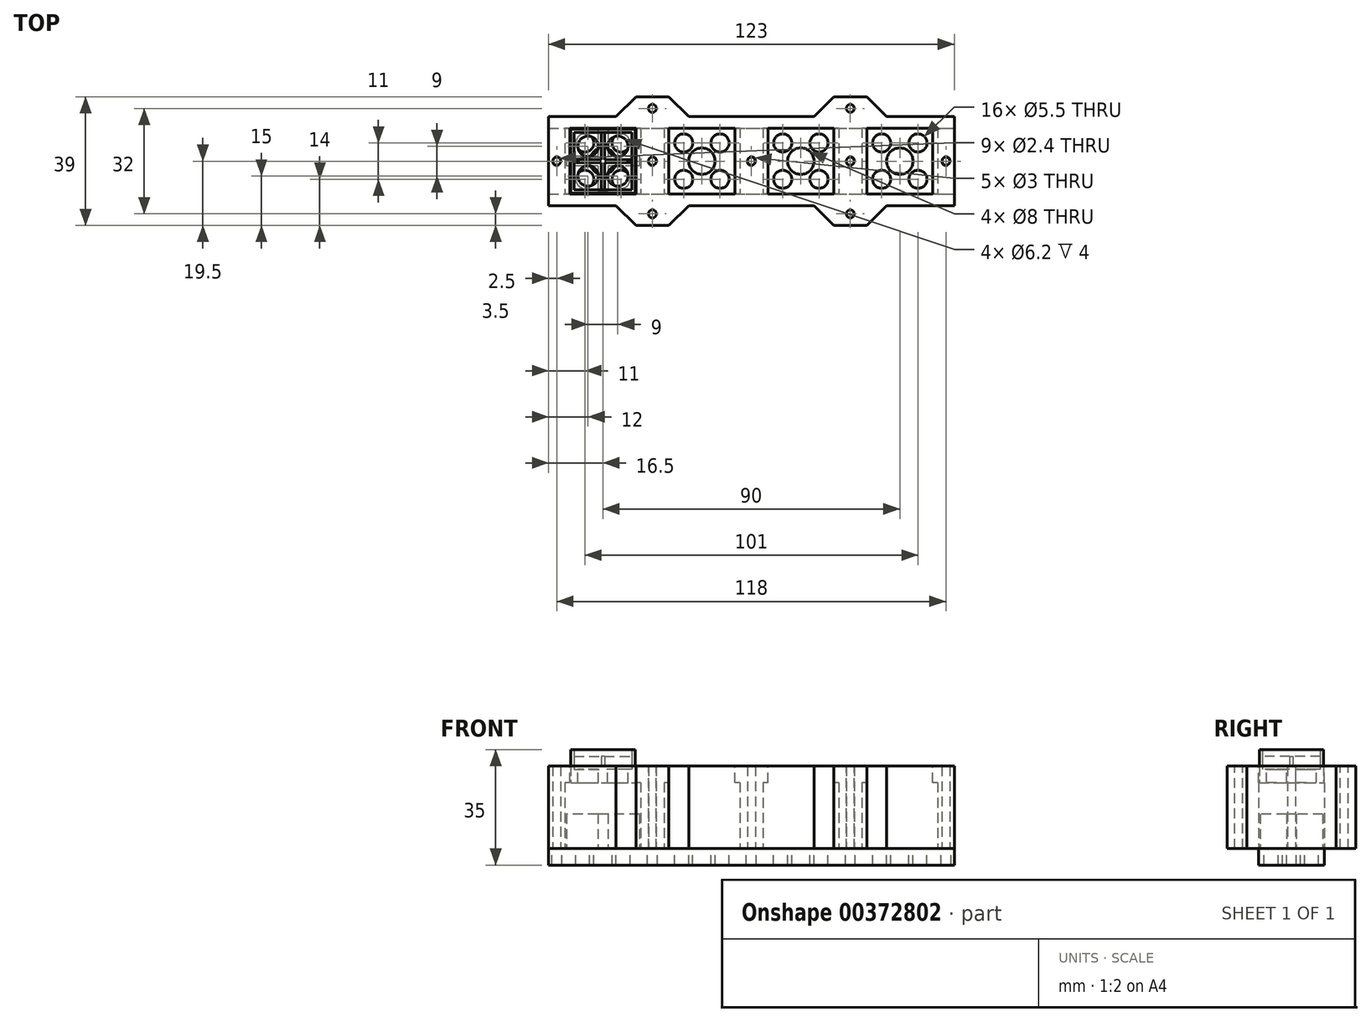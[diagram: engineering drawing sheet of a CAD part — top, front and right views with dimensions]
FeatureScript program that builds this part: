
annotation { "Feature Type Name" : "Feature", "Feature Type Description" : "" }
export const myFeature = defineFeature(function(context is Context, id is Id, definition is map)
    precondition{}
    {
        {
            var Q0;
            Q0=qCreatedBy(makeId("Top.planeOp"),FACE);
            var sketch = newSketch(context, id + "F0", { "sketchPlane" : qUnion([Q0])});
            skPoint(sketch, "E0.middle", {"position": v(0, 0) * mm});
            skLineSegment(sketch, "E1.bottom", {"start": v(9.75, -9.75) * mm, "end": v(-9.75, -9.75) * mm});
            skLineSegment(sketch, "E1.top", {"start": v(9.75, 9.75) * mm, "end": v(-9.75, 9.75) * mm});
            skLineSegment(sketch, "E1.left", {"start": v(9.75, -9.75) * mm, "end": v(9.75, 9.75) * mm});
            skLineSegment(sketch, "E1.right", {"start": v(-9.75, -9.75) * mm, "end": v(-9.75, 9.75) * mm});
            skSolve(sketch);
        }
        {
            var Q0;
            Q0=qSketchRegion(id+"F0",true);
            extrude(context, id + "F1", {"entities" : qUnion([Q0]), "depth" : 13 * mm, "offsetDistance" : 25 * mm});
        }
        {
            var Q0;
            Q0=makeQuery(id+"F1.opExtrude","CAP_FACE",FACE,{"disambiguationData":[OSD([sQuery(id+"F0.wireOp",EDGE,"E1.bottom"),sQuery(id+"F0.wireOp",EDGE,"E1.top"),sQuery(id+"F0.wireOp",EDGE,"E1.left"),sQuery(id+"F0.wireOp",EDGE,"E1.right")])],"isStart":false});
            var sketch = newSketch(context, id + "F2", { "sketchPlane" : qUnion([Q0])});
            skLineSegment(sketch, "E2.bottom", {"start": v(9.75, -9.75) * mm, "end": v(-9.75, -9.75) * mm});
            skLineSegment(sketch, "E2.top", {"start": v(9.75, 9.75) * mm, "end": v(-9.75, 9.75) * mm});
            skLineSegment(sketch, "E2.left", {"start": v(9.75, -9.75) * mm, "end": v(9.75, 9.75) * mm});
            skLineSegment(sketch, "E2.right", {"start": v(-9.75, -9.75) * mm, "end": v(-9.75, 9.75) * mm});
            skPoint(sketch, "E2.middle", {"position": v(0, 0) * mm});
            skLineSegment(sketch, "E3.bottom", {"start": v(8.75, -8.75) * mm, "end": v(-8.75, -8.75) * mm});
            skLineSegment(sketch, "E3.top", {"start": v(8.75, 8.75) * mm, "end": v(-8.75, 8.75) * mm});
            skLineSegment(sketch, "E3.left", {"start": v(8.75, -8.75) * mm, "end": v(8.75, 8.75) * mm});
            skLineSegment(sketch, "E3.right", {"start": v(-8.75, -8.75) * mm, "end": v(-8.75, 8.75) * mm});
            skSolve(sketch);
        }
        {
            var Q0;
            Q0=qSketchRegion(id+"F2",true);
            extrude(context, id + "F3", {"entities" : qUnion([Q0]), "operationType" : NewBodyOperationType.ADD, "depth" : 6 * mm, "offsetDistance" : 25 * mm});
        }
        {
            var Q0;
            Q0=makeQuery(id+"F1.opExtrude","CAP_FACE",FACE,{"disambiguationData":[OSD([sQuery(id+"F0.wireOp",EDGE,"E1.bottom"),sQuery(id+"F0.wireOp",EDGE,"E1.top"),sQuery(id+"F0.wireOp",EDGE,"E1.left"),sQuery(id+"F0.wireOp",EDGE,"E1.right")])],"isStart":false});
            var sketch = newSketch(context, id + "F4", { "sketchPlane" : qUnion([Q0])});
            skLineSegment(sketch, "E4.bottom", {"start": v(-0.5, 8.75) * mm, "end": v(0.5, 8.75) * mm});
            skLineSegment(sketch, "E4.top", {"start": v(-0.5, -8.75) * mm, "end": v(0.5, -8.75) * mm});
            skLineSegment(sketch, "E4.left", {"start": v(-0.5, 8.75) * mm, "end": v(-0.5, 0.5) * mm});
            skLineSegment(sketch, "E4.right", {"start": v(0.5, 8.75) * mm, "end": v(0.5, 0.5) * mm});
            skLineSegment(sketch, "E5.bottom", {"start": v(-8.75, 0.5) * mm, "end": v(-0.5, 0.5) * mm});
            skLineSegment(sketch, "E5.top", {"start": v(-8.75, -0.5) * mm, "end": v(-0.5, -0.5) * mm});
            skLineSegment(sketch, "E5.left", {"start": v(-8.75, 0.5) * mm, "end": v(-8.75, -0.5) * mm});
            skLineSegment(sketch, "E5.right", {"start": v(8.75, 0.5) * mm, "end": v(8.75, -0.5) * mm});
            skLineSegment(sketch, "E6.trimOffspring", {"start": v(-0.5, -0.5) * mm, "end": v(-0.5, -8.75) * mm});
            skLineSegment(sketch, "E7.trimOffspring", {"start": v(0.5, -0.5) * mm, "end": v(0.5, -8.75) * mm});
            skLineSegment(sketch, "E8.trimOffspring", {"start": v(0.5, 0.5) * mm, "end": v(8.75, 0.5) * mm});
            skLineSegment(sketch, "E9.trimOffspring", {"start": v(0.5, -0.5) * mm, "end": v(8.75, -0.5) * mm});
            skSolve(sketch);
        }
        {
            var Q0;
            Q0=qSketchRegion(id+"F4",true);
            extrude(context, id + "F5", {"entities" : qUnion([Q0]), "operationType" : NewBodyOperationType.ADD, "depth" : 4 * mm, "offsetDistance" : 25 * mm});
        }
        {
            var Q0;
            Q0=makeQuery(id+"F1.opExtrude","CAP_FACE",FACE,{"disambiguationData":[OSD([sQuery(id+"F0.wireOp",EDGE,"E1.bottom"),sQuery(id+"F0.wireOp",EDGE,"E1.top"),sQuery(id+"F0.wireOp",EDGE,"E1.left"),sQuery(id+"F0.wireOp",EDGE,"E1.right")])],"isStart":false});
            var sketch = newSketch(context, id + "F6", { "sketchPlane" : qUnion([Q0])});
            skCircle(sketch, "E10", {"center": v(-4.5, 4.5) * mm, "radius": 3.1 * mm});
            skCircle(sketch, "E11", {"center": v(-4.5, -4.5) * mm, "radius": 3.1 * mm});
            skCircle(sketch, "E12", {"center": v(4.5, 4.5) * mm, "radius": 3.1 * mm});
            skCircle(sketch, "E13", {"center": v(4.5, -4.5) * mm, "radius": 3.1 * mm});
            skSolve(sketch);
        }
        {
            var Q0;
            Q0=qSketchRegion(id+"F6",true);
            extrude(context, id + "F7", {"entities" : qUnion([Q0]), "operationType" : NewBodyOperationType.REMOVE, "oppositeDirection" : true, "depth" : 19 * mm, "offsetDistance" : 25 * mm});
        }
        {
            var Q0;
            Q0=makeQuery(id+"F1.opExtrude","CAP_FACE",FACE,{"disambiguationData":[OSD([sQuery(id+"F0.wireOp",EDGE,"E1.bottom"),sQuery(id+"F0.wireOp",EDGE,"E1.top"),sQuery(id+"F0.wireOp",EDGE,"E1.left"),sQuery(id+"F0.wireOp",EDGE,"E1.right")])],"isStart":true});
            var sketch = newSketch(context, id + "F8", { "sketchPlane" : qUnion([Q0])});
            skLineSegment(sketch, "E14.bottom", {"start": v(-9.75, -9.75) * mm, "end": v(-11.25, -9.75) * mm});
            skLineSegment(sketch, "E14.top", {"start": v(-9.75, 9.75) * mm, "end": v(-11.25, 9.75) * mm});
            skLineSegment(sketch, "E14.left", {"start": v(-9.75, -9.75) * mm, "end": v(-9.75, 9.75) * mm});
            skLineSegment(sketch, "E14.right", {"start": v(-11.25, -9.75) * mm, "end": v(-11.25, 9.75) * mm});
            skLineSegment(sketch, "E15.bottom", {"start": v(9.75, -9.75) * mm, "end": v(11.25, -9.75) * mm});
            skLineSegment(sketch, "E15.top", {"start": v(9.75, 9.75) * mm, "end": v(11.25, 9.75) * mm});
            skLineSegment(sketch, "E15.left", {"start": v(9.75, -9.75) * mm, "end": v(9.75, 9.75) * mm});
            skLineSegment(sketch, "E15.right", {"start": v(11.25, -9.75) * mm, "end": v(11.25, 9.75) * mm});
            skSolve(sketch);
        }
        {
            var Q0;
            Q0=qSketchRegion(id+"F8",true);
            extrude(context, id + "F9", {"entities" : qUnion([Q0]), "operationType" : NewBodyOperationType.ADD, "oppositeDirection" : true, "depth" : 9 * mm, "offsetDistance" : 25 * mm});
        }
        {
            var Q0;
            Q0=makeQuery(id+"F9.boolean.opBoolean","MERGE",FACE,{"derivedFrom":[makeQuery(id+"F1.opExtrude","CAP_FACE",FACE,{"disambiguationData":[OSD([sQuery(id+"F0.wireOp",EDGE,"E1.bottom"),sQuery(id+"F0.wireOp",EDGE,"E1.top"),sQuery(id+"F0.wireOp",EDGE,"E1.left"),sQuery(id+"F0.wireOp",EDGE,"E1.right")])],"isStart":true}),makeQuery(id+"F9.opExtrude","CAP_FACE",FACE,{"disambiguationData":[OSD([sQuery(id+"F8.wireOp",EDGE,"E14.bottom"),sQuery(id+"F8.wireOp",EDGE,"E14.top"),sQuery(id+"F8.wireOp",EDGE,"E14.left"),sQuery(id+"F8.wireOp",EDGE,"E14.right")])],"isStart":true}),makeQuery(id+"F9.opExtrude","CAP_FACE",FACE,{"disambiguationData":[OSD([sQuery(id+"F8.wireOp",EDGE,"E15.bottom"),sQuery(id+"F8.wireOp",EDGE,"E15.top"),sQuery(id+"F8.wireOp",EDGE,"E15.left"),sQuery(id+"F8.wireOp",EDGE,"E15.right")])],"isStart":true})]});
            var sketch = newSketch(context, id + "F10", { "sketchPlane" : qUnion([Q0])});
            skCircle(sketch, "E16", {"center": v(0, 0) * mm, "radius": 2.55 * mm});
            skSolve(sketch);
        }
        {
            var Q0;
            Q0=qSketchRegion(id+"F10",true);
            extrude(context, id + "F11", {"entities" : qUnion([Q0]), "operationType" : NewBodyOperationType.REMOVE, "oppositeDirection" : true, "depth" : 3 * mm, "offsetDistance" : 25 * mm});
        }
        {
            var Q0;
            Q0=qCreatedBy(makeId("Top.planeOp"),FACE);
            cPlane(context, id + "F12", {"entities" : qUnion([Q0]), "cplaneType" : CPlaneType.OFFSET, "offset" : 14 * mm, "width" : 150 * mm, "height" : 150 * mm});
        }
        {
            var Q0;
            Q0=qCreatedBy(id+"F12.planeOp",FACE);
            var sketch = newSketch(context, id + "F13", { "sketchPlane" : qUnion([Q0])});
            skPoint(sketch, "E17.middle", {"position": v(0, 0) * mm});
            skLineSegment(sketch, "E18.bottom", {"start": v(10, -10) * mm, "end": v(-10, -10) * mm});
            skLineSegment(sketch, "E18.top", {"start": v(10, 10) * mm, "end": v(-10, 10) * mm});
            skLineSegment(sketch, "E18.left", {"start": v(10, -10) * mm, "end": v(10, 10) * mm});
            skLineSegment(sketch, "E18.right", {"start": v(-10, -10) * mm, "end": v(-10, 10) * mm});
            skLineSegment(sketch, "E19.bottom", {"start": v(40, -10) * mm, "end": v(20, -10) * mm});
            skLineSegment(sketch, "E19.top", {"start": v(40, 10) * mm, "end": v(20, 10) * mm});
            skLineSegment(sketch, "E19.left", {"start": v(40, -10) * mm, "end": v(40, 10) * mm});
            skLineSegment(sketch, "E19.right", {"start": v(20, -10) * mm, "end": v(20, 10) * mm});
            skPoint(sketch, "E19.middle", {"position": v(30, 0) * mm});
            skLineSegment(sketch, "E20.bottom", {"start": v(70, -10) * mm, "end": v(50, -10) * mm});
            skLineSegment(sketch, "E20.top", {"start": v(70, 10) * mm, "end": v(50, 10) * mm});
            skLineSegment(sketch, "E20.left", {"start": v(70, -10) * mm, "end": v(70, 10) * mm});
            skLineSegment(sketch, "E20.right", {"start": v(50, -10) * mm, "end": v(50, 10) * mm});
            skPoint(sketch, "E20.middle", {"position": v(60, 0) * mm});
            skLineSegment(sketch, "E21.bottom", {"start": v(100, -10) * mm, "end": v(80, -10) * mm});
            skLineSegment(sketch, "E21.top", {"start": v(100, 10) * mm, "end": v(80, 10) * mm});
            skLineSegment(sketch, "E21.left", {"start": v(100, -10) * mm, "end": v(100, 10) * mm});
            skLineSegment(sketch, "E21.right", {"start": v(80, -10) * mm, "end": v(80, 10) * mm});
            skPoint(sketch, "E21.middle", {"position": v(90, 0) * mm});
            skLineSegment(sketch, "E22.bottom", {"start": v(10, 13.5) * mm, "end": v(20, 13.5) * mm});
            skLineSegment(sketch, "E22.top", {"start": v(10, 19.5) * mm, "end": v(20, 19.5) * mm});
            skLineSegment(sketch, "E22.left", {"start": v(10, 13.5) * mm, "end": v(10, 19.5) * mm});
            skLineSegment(sketch, "E22.right", {"start": v(20, 13.5) * mm, "end": v(20, 19.5) * mm});
            skLineSegment(sketch, "E23.bottom", {"start": v(10, -13.5) * mm, "end": v(20, -13.5) * mm});
            skLineSegment(sketch, "E23.top", {"start": v(10, -19.5) * mm, "end": v(20, -19.5) * mm});
            skLineSegment(sketch, "E23.left", {"start": v(10, -13.5) * mm, "end": v(10, -19.5) * mm});
            skLineSegment(sketch, "E23.right", {"start": v(20, -13.5) * mm, "end": v(20, -19.5) * mm});
            skLineSegment(sketch, "E24.bottom", {"start": v(106.5, -13.5) * mm, "end": v(-16.5, -13.5) * mm});
            skLineSegment(sketch, "E24.top", {"start": v(106.5, 13.5) * mm, "end": v(-16.5, 13.5) * mm});
            skLineSegment(sketch, "E24.left", {"start": v(106.5, -13.5) * mm, "end": v(106.5, 13.5) * mm});
            skLineSegment(sketch, "E24.right", {"start": v(-16.5, -13.5) * mm, "end": v(-16.5, 13.5) * mm});
            skPoint(sketch, "E24.middle", {"position": v(45, 0) * mm});
            skLineSegment(sketch, "E25.bottom", {"start": v(70, 13.5) * mm, "end": v(80, 13.5) * mm});
            skLineSegment(sketch, "E25.top", {"start": v(70, 19.5) * mm, "end": v(80, 19.5) * mm});
            skLineSegment(sketch, "E25.left", {"start": v(70, 13.5) * mm, "end": v(70, 19.5) * mm});
            skLineSegment(sketch, "E25.right", {"start": v(80, 13.5) * mm, "end": v(80, 19.5) * mm});
            skLineSegment(sketch, "E26.bottom", {"start": v(70, -13.5) * mm, "end": v(80, -13.5) * mm});
            skLineSegment(sketch, "E26.top", {"start": v(70, -19.5) * mm, "end": v(80, -19.5) * mm});
            skLineSegment(sketch, "E26.left", {"start": v(70, -13.5) * mm, "end": v(70, -19.5) * mm});
            skLineSegment(sketch, "E26.right", {"start": v(80, -13.5) * mm, "end": v(80, -19.5) * mm});
            skSolve(sketch);
        }
        {
            var Q0;
            Q0=qSketchRegion(id+"F13",true);
            extrude(context, id + "F14", {"entities" : qUnion([Q0]), "oppositeDirection" : true, "depth" : 25 * mm, "offsetDistance" : 25 * mm});
        }
        {
            var Q0;
            Q0=makeQuery(id+"F14.opExtrude","CAP_FACE",FACE,{"disambiguationData":[OSD([sQuery(id+"F13.wireOp",EDGE,"E17.bottom"),sQuery(id+"F13.wireOp",EDGE,"E17.top"),sQuery(id+"F13.wireOp",EDGE,"E17.left"),sQuery(id+"F13.wireOp",EDGE,"E17.right"),sQuery(id+"F13.wireOp",EDGE,"E18.bottom"),sQuery(id+"F13.wireOp",EDGE,"E18.top"),sQuery(id+"F13.wireOp",EDGE,"E18.left"),sQuery(id+"F13.wireOp",EDGE,"E18.right")])],"isStart":false});
            var sketch = newSketch(context, id + "F15", { "sketchPlane" : qUnion([Q0])});
            skLineSegment(sketch, "E27.bottom", {"start": v(11.5, -10) * mm, "end": v(-11.5, -10) * mm});
            skLineSegment(sketch, "E27.top", {"start": v(11.5, 10) * mm, "end": v(-11.5, 10) * mm});
            skLineSegment(sketch, "E27.left", {"start": v(11.5, -10) * mm, "end": v(11.5, 10) * mm});
            skLineSegment(sketch, "E27.right", {"start": v(-11.5, -10) * mm, "end": v(-11.5, 10) * mm});
            skPoint(sketch, "E27.middle", {"position": v(0, 0) * mm});
            skLineSegment(sketch, "E28.bottom", {"start": v(41.5, -10) * mm, "end": v(18.5, -10) * mm});
            skLineSegment(sketch, "E28.top", {"start": v(41.5, 10) * mm, "end": v(18.5, 10) * mm});
            skLineSegment(sketch, "E28.left", {"start": v(41.5, -10) * mm, "end": v(41.5, 10) * mm});
            skLineSegment(sketch, "E28.right", {"start": v(18.5, -10) * mm, "end": v(18.5, 10) * mm});
            skPoint(sketch, "E28.middle", {"position": v(30, 0) * mm});
            skPoint(sketch, "E28.middle.positionSnap0", {"position": v(20, 0) * mm});
            skPoint(sketch, "E28.middle.positionSnap1", {"position": v(30, 10) * mm});
            skPoint(sketch, "E28.centerSnap0", {"position": v(20, 0) * mm});
            skPoint(sketch, "E28.centerSnap1", {"position": v(30, 10) * mm});
            skLineSegment(sketch, "E29.bottom", {"start": v(71.5, -10) * mm, "end": v(48.5, -10) * mm});
            skLineSegment(sketch, "E29.top", {"start": v(71.5, 10) * mm, "end": v(48.5, 10) * mm});
            skLineSegment(sketch, "E29.left", {"start": v(71.5, -10) * mm, "end": v(71.5, 10) * mm});
            skLineSegment(sketch, "E29.right", {"start": v(48.5, -10) * mm, "end": v(48.5, 10) * mm});
            skPoint(sketch, "E29.middle", {"position": v(60, 0) * mm});
            skPoint(sketch, "E29.middle.positionSnap0", {"position": v(50, 0) * mm});
            skPoint(sketch, "E29.middle.positionSnap1", {"position": v(60, 10) * mm});
            skPoint(sketch, "E29.centerSnap0", {"position": v(50, 0) * mm});
            skPoint(sketch, "E29.centerSnap1", {"position": v(60, 10) * mm});
            skLineSegment(sketch, "E30.bottom", {"start": v(101.5, -10) * mm, "end": v(78.5, -10) * mm});
            skLineSegment(sketch, "E30.top", {"start": v(101.5, 10) * mm, "end": v(78.5, 10) * mm});
            skLineSegment(sketch, "E30.left", {"start": v(101.5, -10) * mm, "end": v(101.5, 10) * mm});
            skLineSegment(sketch, "E30.right", {"start": v(78.5, -10) * mm, "end": v(78.5, 10) * mm});
            skPoint(sketch, "E30.middle", {"position": v(90, 0) * mm});
            skPoint(sketch, "E30.middle.positionSnap0", {"position": v(90, 10) * mm});
            skPoint(sketch, "E30.centerSnap0", {"position": v(90, 10) * mm});
            skSolve(sketch);
        }
        {
            var Q0;
            Q0=qSketchRegion(id+"F15",true);
            extrude(context, id + "F16", {"entities" : qUnion([Q0]), "operationType" : NewBodyOperationType.REMOVE, "oppositeDirection" : true, "depth" : 20 * mm, "offsetDistance" : 25 * mm});
        }
        {
            var Q0;
            Q0=makeQuery(id+"F14.opExtrude","CAP_FACE",FACE,{"disambiguationData":[OSD([sQuery(id+"F13.wireOp",EDGE,"E18.bottom"),sQuery(id+"F13.wireOp",EDGE,"E18.top"),sQuery(id+"F13.wireOp",EDGE,"E18.left"),sQuery(id+"F13.wireOp",EDGE,"E18.right"),sQuery(id+"F13.wireOp",EDGE,"E19.bottom"),sQuery(id+"F13.wireOp",EDGE,"E19.top"),sQuery(id+"F13.wireOp",EDGE,"E19.left"),sQuery(id+"F13.wireOp",EDGE,"E19.right"),sQuery(id+"F13.wireOp",EDGE,"E20.bottom"),sQuery(id+"F13.wireOp",EDGE,"E20.top"),sQuery(id+"F13.wireOp",EDGE,"E20.left"),sQuery(id+"F13.wireOp",EDGE,"E20.right"),sQuery(id+"F13.wireOp",EDGE,"E21.bottom"),sQuery(id+"F13.wireOp",EDGE,"E21.top"),sQuery(id+"F13.wireOp",EDGE,"E21.left"),sQuery(id+"F13.wireOp",EDGE,"E21.right"),sQuery(id+"F13.wireOp",EDGE,"E22.top"),sQuery(id+"F13.wireOp",EDGE,"E22.left"),sQuery(id+"F13.wireOp",EDGE,"E22.right"),sQuery(id+"F13.wireOp",EDGE,"E23.top"),sQuery(id+"F13.wireOp",EDGE,"E23.left"),sQuery(id+"F13.wireOp",EDGE,"E23.right"),sQuery(id+"F13.wireOp",EDGE,"E24.bottom"),sQuery(id+"F13.wireOp",EDGE,"E24.top"),sQuery(id+"F13.wireOp",EDGE,"E24.left"),sQuery(id+"F13.wireOp",EDGE,"E24.right"),sQuery(id+"F13.wireOp",EDGE,"E25.top"),sQuery(id+"F13.wireOp",EDGE,"E25.left"),sQuery(id+"F13.wireOp",EDGE,"E25.right"),sQuery(id+"F13.wireOp",EDGE,"E26.top"),sQuery(id+"F13.wireOp",EDGE,"E26.left"),sQuery(id+"F13.wireOp",EDGE,"E26.right")])],"isStart":true});
            var sketch = newSketch(context, id + "F17", { "sketchPlane" : qUnion([Q0])});
            skCircle(sketch, "E31", {"center": v(15, 16) * mm, "radius": 1.2 * mm});
            skPoint(sketch, "E31.centerSnap0", {"position": v(15, 19.5) * mm});
            skCircle(sketch, "E32", {"center": v(15, -16) * mm, "radius": 1.2 * mm});
            skCircle(sketch, "E33", {"center": v(75, 16) * mm, "radius": 1.2 * mm});
            skPoint(sketch, "E33.centerSnap0", {"position": v(75, 19.5) * mm});
            skCircle(sketch, "E34", {"center": v(75, -16) * mm, "radius": 1.2 * mm});
            skSolve(sketch);
        }
        {
            var Q0;
            Q0=qSketchRegion(id+"F17",true);
            extrude(context, id + "F18", {"entities" : qUnion([Q0]), "operationType" : NewBodyOperationType.REMOVE, "oppositeDirection" : true, "depth" : 30 * mm, "offsetDistance" : 25 * mm});
        }
        {
            var Q0;
            Q0=makeQuery(id+"F14.opExtrude","CAP_FACE",FACE,{"disambiguationData":[OSD([sQuery(id+"F13.wireOp",EDGE,"E18.bottom"),sQuery(id+"F13.wireOp",EDGE,"E18.top"),sQuery(id+"F13.wireOp",EDGE,"E18.left"),sQuery(id+"F13.wireOp",EDGE,"E18.right"),sQuery(id+"F13.wireOp",EDGE,"E19.bottom"),sQuery(id+"F13.wireOp",EDGE,"E19.top"),sQuery(id+"F13.wireOp",EDGE,"E19.left"),sQuery(id+"F13.wireOp",EDGE,"E19.right"),sQuery(id+"F13.wireOp",EDGE,"E20.bottom"),sQuery(id+"F13.wireOp",EDGE,"E20.top"),sQuery(id+"F13.wireOp",EDGE,"E20.left"),sQuery(id+"F13.wireOp",EDGE,"E20.right"),sQuery(id+"F13.wireOp",EDGE,"E21.bottom"),sQuery(id+"F13.wireOp",EDGE,"E21.top"),sQuery(id+"F13.wireOp",EDGE,"E21.left"),sQuery(id+"F13.wireOp",EDGE,"E21.right"),sQuery(id+"F13.wireOp",EDGE,"E22.top"),sQuery(id+"F13.wireOp",EDGE,"E22.left"),sQuery(id+"F13.wireOp",EDGE,"E22.right"),sQuery(id+"F13.wireOp",EDGE,"E23.top"),sQuery(id+"F13.wireOp",EDGE,"E23.left"),sQuery(id+"F13.wireOp",EDGE,"E23.right"),sQuery(id+"F13.wireOp",EDGE,"E24.bottom"),sQuery(id+"F13.wireOp",EDGE,"E24.top"),sQuery(id+"F13.wireOp",EDGE,"E24.left"),sQuery(id+"F13.wireOp",EDGE,"E24.right"),sQuery(id+"F13.wireOp",EDGE,"E25.top"),sQuery(id+"F13.wireOp",EDGE,"E25.left"),sQuery(id+"F13.wireOp",EDGE,"E25.right"),sQuery(id+"F13.wireOp",EDGE,"E26.top"),sQuery(id+"F13.wireOp",EDGE,"E26.left"),sQuery(id+"F13.wireOp",EDGE,"E26.right")])],"isStart":false});
            var sketch = newSketch(context, id + "F19", { "sketchPlane" : qUnion([Q0])});
            skCircle(sketch, "E35", {"center": v(-14, 0) * mm, "radius": 1.2 * mm});
            skCircle(sketch, "E36", {"center": v(15, 0) * mm, "radius": 1.2 * mm});
            skCircle(sketch, "E37", {"center": v(45, 0) * mm, "radius": 1.2 * mm});
            skCircle(sketch, "E38", {"center": v(75, 0) * mm, "radius": 1.2 * mm});
            skCircle(sketch, "E39", {"center": v(104, 0) * mm, "radius": 1.2 * mm});
            skSolve(sketch);
        }
        {
            var Q0;
            Q0=qSketchRegion(id+"F19",true);
            extrude(context, id + "F20", {"entities" : qUnion([Q0]), "operationType" : NewBodyOperationType.REMOVE, "endBound" : BoundingType.THROUGH_ALL, "oppositeDirection" : true, "depth" : 10 * mm, "offsetDistance" : 25 * mm});
        }
        {
            var Q0;
            Q0=makeQuery(id+"F14.opExtrude","CAP_FACE",FACE,{"disambiguationData":[OSD([sQuery(id+"F13.wireOp",EDGE,"E18.bottom"),sQuery(id+"F13.wireOp",EDGE,"E18.top"),sQuery(id+"F13.wireOp",EDGE,"E18.left"),sQuery(id+"F13.wireOp",EDGE,"E18.right"),sQuery(id+"F13.wireOp",EDGE,"E19.bottom"),sQuery(id+"F13.wireOp",EDGE,"E19.top"),sQuery(id+"F13.wireOp",EDGE,"E19.left"),sQuery(id+"F13.wireOp",EDGE,"E19.right"),sQuery(id+"F13.wireOp",EDGE,"E20.bottom"),sQuery(id+"F13.wireOp",EDGE,"E20.top"),sQuery(id+"F13.wireOp",EDGE,"E20.left"),sQuery(id+"F13.wireOp",EDGE,"E20.right"),sQuery(id+"F13.wireOp",EDGE,"E21.bottom"),sQuery(id+"F13.wireOp",EDGE,"E21.top"),sQuery(id+"F13.wireOp",EDGE,"E21.left"),sQuery(id+"F13.wireOp",EDGE,"E21.right"),sQuery(id+"F13.wireOp",EDGE,"E22.top"),sQuery(id+"F13.wireOp",EDGE,"E22.left"),sQuery(id+"F13.wireOp",EDGE,"E22.right"),sQuery(id+"F13.wireOp",EDGE,"E23.top"),sQuery(id+"F13.wireOp",EDGE,"E23.left"),sQuery(id+"F13.wireOp",EDGE,"E23.right"),sQuery(id+"F13.wireOp",EDGE,"E24.bottom"),sQuery(id+"F13.wireOp",EDGE,"E24.top"),sQuery(id+"F13.wireOp",EDGE,"E24.left"),sQuery(id+"F13.wireOp",EDGE,"E24.right"),sQuery(id+"F13.wireOp",EDGE,"E25.top"),sQuery(id+"F13.wireOp",EDGE,"E25.left"),sQuery(id+"F13.wireOp",EDGE,"E25.right"),sQuery(id+"F13.wireOp",EDGE,"E26.top"),sQuery(id+"F13.wireOp",EDGE,"E26.left"),sQuery(id+"F13.wireOp",EDGE,"E26.right")])],"isStart":false});
            var sketch = newSketch(context, id + "F21", { "sketchPlane" : qUnion([Q0])});
            skCircle(sketch, "E40", {"center": v(-14, 0) * mm, "radius": 1.5 * mm});
            skCircle(sketch, "E41", {"center": v(15, 0) * mm, "radius": 1.5 * mm});
            skCircle(sketch, "E42", {"center": v(45, 0) * mm, "radius": 1.5 * mm});
            skCircle(sketch, "E43", {"center": v(75, 0) * mm, "radius": 1.5 * mm});
            skCircle(sketch, "E44", {"center": v(104, 0) * mm, "radius": 1.5 * mm});
            skCircle(sketch, "E45", {"center": v(0, 0) * mm, "radius": 4 * mm});
            skCircle(sketch, "E46", {"center": v(-5.5, 5.5) * mm, "radius": 2.75 * mm});
            skCircle(sketch, "E47", {"center": v(5.5, 5.5) * mm, "radius": 2.75 * mm});
            skCircle(sketch, "E48", {"center": v(-5.5, -5.5) * mm, "radius": 2.75 * mm});
            skCircle(sketch, "E49", {"center": v(5.5, -5.5) * mm, "radius": 2.75 * mm});
            skCircle(sketch, "E50.1.0.0", {"center": v(30, 0) * mm, "radius": 4 * mm});
            skCircle(sketch, "E50.1.0.1", {"center": v(35.5, -5.5) * mm, "radius": 2.75 * mm});
            skCircle(sketch, "E50.1.0.2", {"center": v(35.5, 5.5) * mm, "radius": 2.75 * mm});
            skCircle(sketch, "E50.1.0.3", {"center": v(24.5, 5.5) * mm, "radius": 2.75 * mm});
            skCircle(sketch, "E50.1.0.4", {"center": v(24.5, -5.5) * mm, "radius": 2.75 * mm});
            skCircle(sketch, "E50.2.0.0", {"center": v(60, 0) * mm, "radius": 4 * mm});
            skCircle(sketch, "E50.2.0.1", {"center": v(65.5, -5.5) * mm, "radius": 2.75 * mm});
            skCircle(sketch, "E50.2.0.2", {"center": v(65.5, 5.5) * mm, "radius": 2.75 * mm});
            skCircle(sketch, "E50.2.0.3", {"center": v(54.5, 5.5) * mm, "radius": 2.75 * mm});
            skCircle(sketch, "E50.2.0.4", {"center": v(54.5, -5.5) * mm, "radius": 2.75 * mm});
            skLineSegment(sketch, "E50.direction1", {"start": v(-5.5, -5.5) * mm, "end": v(24.5, -5.5) * mm, "construction": true});
            skCircle(sketch, "E51.0.3.0", {"center": v(90, 0) * mm, "radius": 4 * mm});
            skCircle(sketch, "E51.2.3.0", {"center": v(95.5, -5.5) * mm, "radius": 2.75 * mm});
            skCircle(sketch, "E51.4.3.0", {"center": v(95.5, 5.5) * mm, "radius": 2.75 * mm});
            skCircle(sketch, "E51.6.3.0", {"center": v(84.5, 5.5) * mm, "radius": 2.75 * mm});
            skCircle(sketch, "E51.8.3.0", {"center": v(84.5, -5.5) * mm, "radius": 2.75 * mm});
            skLineSegment(sketch, "E52.bottom", {"start": v(-16.5, -10) * mm, "end": v(106.5, -10) * mm});
            skLineSegment(sketch, "E52.top", {"start": v(-16.5, 10) * mm, "end": v(106.5, 10) * mm});
            skLineSegment(sketch, "E52.left", {"start": v(-16.5, -10) * mm, "end": v(-16.5, 10) * mm});
            skLineSegment(sketch, "E52.right", {"start": v(106.5, -10) * mm, "end": v(106.5, 10) * mm});
            skSolve(sketch);
        }
        {
            var Q0;
            Q0=qSketchRegion(id+"F21",true);
            extrude(context, id + "F22", {"entities" : qUnion([Q0]), "depth" : 5 * mm, "offsetDistance" : 25 * mm});
        }
        {
            var Q0;
            Q0=makeQuery(id+"F14.opExtrude","SWEPT_EDGE",EDGE,{"disambiguationData":[OSD([sQuery(id+"F13.wireOp",EDGE,"E23.left"),sQuery(id+"F13.wireOp",EDGE,"E24.bottom")])]});
            var Q1;
            Q1=makeQuery(id+"F14.opExtrude","SWEPT_EDGE",EDGE,{"disambiguationData":[OSD([sQuery(id+"F13.wireOp",EDGE,"E23.right"),sQuery(id+"F13.wireOp",EDGE,"E24.bottom")])]});
            var Q2;
            Q2=makeQuery(id+"F14.opExtrude","SWEPT_EDGE",EDGE,{"disambiguationData":[OSD([sQuery(id+"F13.wireOp",EDGE,"E24.bottom"),sQuery(id+"F13.wireOp",EDGE,"E26.bottom"),sQuery(id+"F13.wireOp",EDGE,"E26.left")])]});
            var Q3;
            Q3=makeQuery(id+"F14.opExtrude","SWEPT_EDGE",EDGE,{"disambiguationData":[OSD([sQuery(id+"F13.wireOp",EDGE,"E24.bottom"),sQuery(id+"F13.wireOp",EDGE,"E26.bottom"),sQuery(id+"F13.wireOp",EDGE,"E26.right")])]});
            var Q4;
            Q4=makeQuery(id+"F14.opExtrude","SWEPT_EDGE",EDGE,{"disambiguationData":[OSD([sQuery(id+"F13.wireOp",EDGE,"E22.left"),sQuery(id+"F13.wireOp",EDGE,"E24.top")])]});
            var Q5;
            Q5=makeQuery(id+"F14.opExtrude","SWEPT_EDGE",EDGE,{"disambiguationData":[OSD([sQuery(id+"F13.wireOp",EDGE,"E22.right"),sQuery(id+"F13.wireOp",EDGE,"E24.top")])]});
            var Q6;
            Q6=makeQuery(id+"F14.opExtrude","SWEPT_EDGE",EDGE,{"disambiguationData":[OSD([sQuery(id+"F13.wireOp",EDGE,"E24.top"),sQuery(id+"F13.wireOp",EDGE,"E25.bottom"),sQuery(id+"F13.wireOp",EDGE,"E25.left")])]});
            var Q7;
            Q7=makeQuery(id+"F14.opExtrude","SWEPT_EDGE",EDGE,{"disambiguationData":[OSD([sQuery(id+"F13.wireOp",EDGE,"E24.top"),sQuery(id+"F13.wireOp",EDGE,"E25.bottom"),sQuery(id+"F13.wireOp",EDGE,"E25.right")])]});
            chamfer(context, id + "F23", {"entities" : qUnion([Q0, Q1, Q2, Q3, Q4, Q5, Q6, Q7]), "width" : 6 * mm, "tangentPropagation" : true});
        }
        {
            var Q0;
            Q0=makeQuery(id+"F14.opExtrude","CAP_FACE",FACE,{"disambiguationData":[OSD([sQuery(id+"F13.wireOp",EDGE,"E18.bottom"),sQuery(id+"F13.wireOp",EDGE,"E18.top"),sQuery(id+"F13.wireOp",EDGE,"E18.left"),sQuery(id+"F13.wireOp",EDGE,"E18.right"),sQuery(id+"F13.wireOp",EDGE,"E19.bottom"),sQuery(id+"F13.wireOp",EDGE,"E19.top"),sQuery(id+"F13.wireOp",EDGE,"E19.left"),sQuery(id+"F13.wireOp",EDGE,"E19.right"),sQuery(id+"F13.wireOp",EDGE,"E20.bottom"),sQuery(id+"F13.wireOp",EDGE,"E20.top"),sQuery(id+"F13.wireOp",EDGE,"E20.left"),sQuery(id+"F13.wireOp",EDGE,"E20.right"),sQuery(id+"F13.wireOp",EDGE,"E21.bottom"),sQuery(id+"F13.wireOp",EDGE,"E21.top"),sQuery(id+"F13.wireOp",EDGE,"E21.left"),sQuery(id+"F13.wireOp",EDGE,"E21.right"),sQuery(id+"F13.wireOp",EDGE,"E22.top"),sQuery(id+"F13.wireOp",EDGE,"E22.left"),sQuery(id+"F13.wireOp",EDGE,"E22.right"),sQuery(id+"F13.wireOp",EDGE,"E23.top"),sQuery(id+"F13.wireOp",EDGE,"E23.left"),sQuery(id+"F13.wireOp",EDGE,"E23.right"),sQuery(id+"F13.wireOp",EDGE,"E24.bottom"),sQuery(id+"F13.wireOp",EDGE,"E24.top"),sQuery(id+"F13.wireOp",EDGE,"E24.left"),sQuery(id+"F13.wireOp",EDGE,"E24.right"),sQuery(id+"F13.wireOp",EDGE,"E25.top"),sQuery(id+"F13.wireOp",EDGE,"E25.left"),sQuery(id+"F13.wireOp",EDGE,"E25.right"),sQuery(id+"F13.wireOp",EDGE,"E26.top"),sQuery(id+"F13.wireOp",EDGE,"E26.left"),sQuery(id+"F13.wireOp",EDGE,"E26.right")])],"isStart":false});
            cPlane(context, id + "F24", {"entities" : qUnion([Q0]), "cplaneType" : CPlaneType.OFFSET, "offset" : 0 * mm, "width" : 150 * mm, "height" : 150 * mm});
        }
        {
            var Q0;
            Q0=qCreatedBy(id+"F24.planeOp",FACE);
            var sketch = newSketch(context, id + "F25", { "sketchPlane" : qUnion([Q0])});
            skLineSegment(sketch, "E53.bottom", {"start": v(1.5, -9.5) * mm, "end": v(-1.5, -9.5) * mm});
            skLineSegment(sketch, "E53.top", {"start": v(1.5, 9.5) * mm, "end": v(-1.5, 9.5) * mm});
            skLineSegment(sketch, "E53.left", {"start": v(1.5, -9.5) * mm, "end": v(1.5, 9.5) * mm});
            skLineSegment(sketch, "E53.right", {"start": v(-1.5, -9.5) * mm, "end": v(-1.5, 9.5) * mm});
            skPoint(sketch, "E53.middle", {"position": v(0, 0) * mm});
            skLineSegment(sketch, "E54.bottom", {"start": v(11, -1.5) * mm, "end": v(-11, -1.5) * mm});
            skLineSegment(sketch, "E54.top", {"start": v(11, 1.5) * mm, "end": v(-11, 1.5) * mm});
            skLineSegment(sketch, "E54.left", {"start": v(11, -1.5) * mm, "end": v(11, 1.5) * mm});
            skLineSegment(sketch, "E54.right", {"start": v(-11, -1.5) * mm, "end": v(-11, 1.5) * mm});
            skLineSegment(sketch, "E55.0", {"start": v(11.5, 10) * mm, "end": v(-11.5, 10) * mm});
            skLineSegment(sketch, "E55.1", {"start": v(11.5, -10) * mm, "end": v(11.5, 10) * mm});
            skPoint(sketch, "E56", {"position": v(11.5, 0) * mm});
            skPoint(sketch, "E57", {"position": v(0, 10) * mm});
            skSolve(sketch);
        }
        {
            var Q0;
            Q0=qSketchRegion(id+"F25",true);
            extrude(context, id + "F26", {"entities" : qUnion([Q0]), "oppositeDirection" : true, "depth" : 10.5 * mm, "offsetDistance" : 25 * mm});
        }
    });
